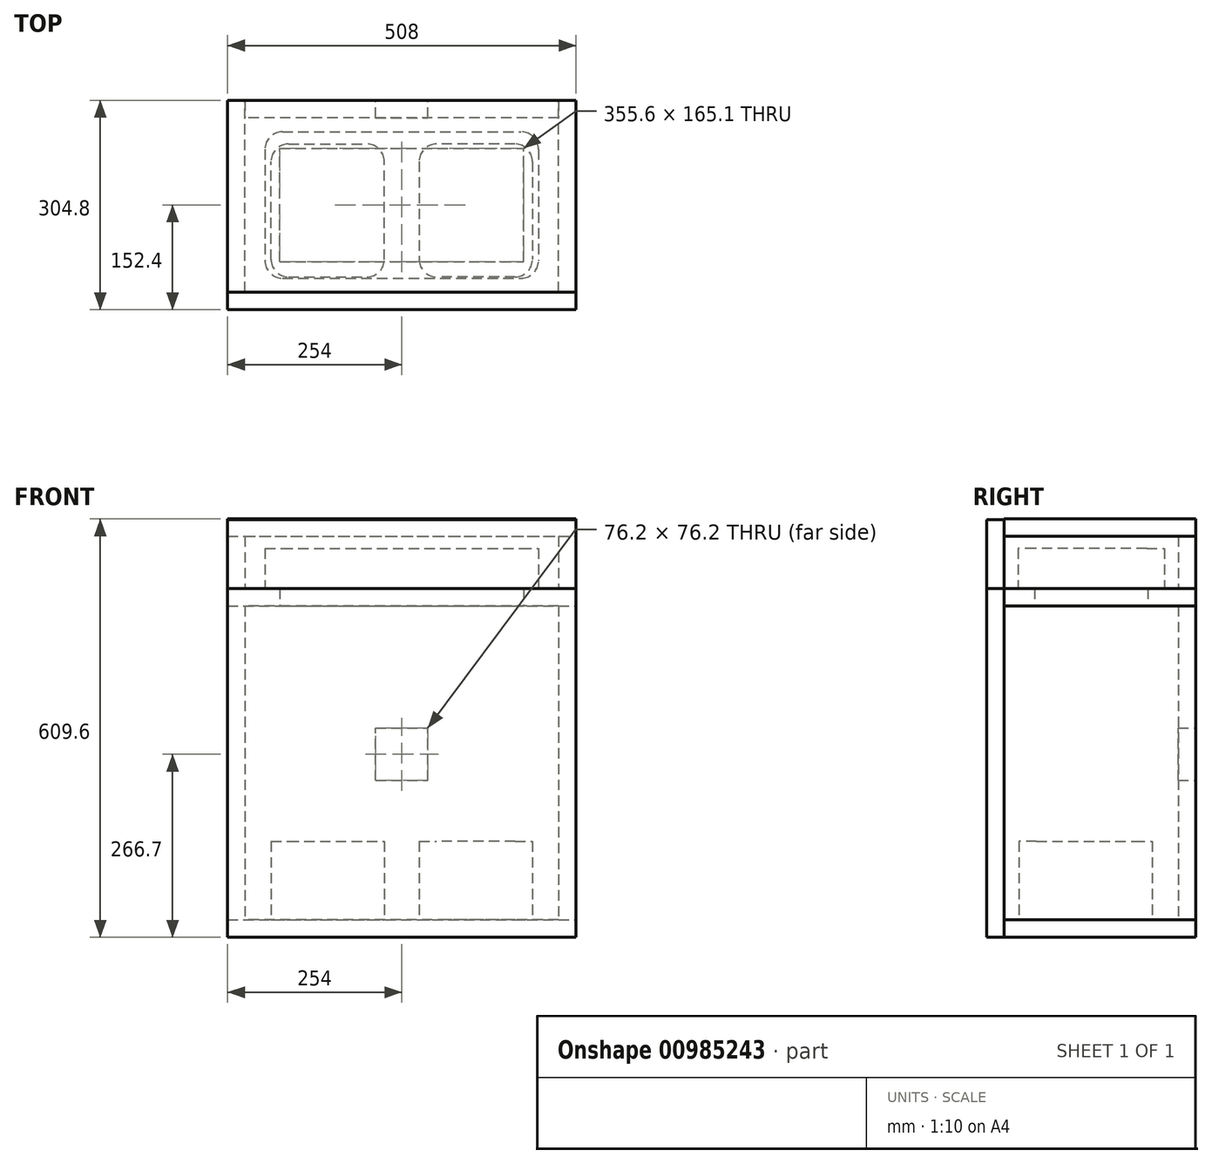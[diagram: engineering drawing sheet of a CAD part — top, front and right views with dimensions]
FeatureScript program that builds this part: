
annotation { "Feature Type Name" : "Feature", "Feature Type Description" : "" }
export const myFeature = defineFeature(function(context is Context, id is Id, definition is map)
    precondition{}
    {
        {
            var Q0;
            Q0=qCreatedBy(makeId("Top.planeOp"),FACE);
            var sketch = newSketch(context, id + "F0", { "sketchPlane" : qUnion([Q0])});
            skLineSegment(sketch, "E0.bottom", {"start": v(0, 0) * mm, "end": v(508, 0) * mm});
            skLineSegment(sketch, "E0.top", {"start": v(0, 279.4) * mm, "end": v(508, 279.4) * mm});
            skLineSegment(sketch, "E0.left", {"start": v(0, 0) * mm, "end": v(0, 279.4) * mm});
            skLineSegment(sketch, "E0.right", {"start": v(508, 0) * mm, "end": v(508, 279.4) * mm});
            skLineSegment(sketch, "E1.bottom", {"start": v(76.2, 44.45) * mm, "end": v(431.8, 44.45) * mm});
            skLineSegment(sketch, "E1.top", {"start": v(76.2, 209.55) * mm, "end": v(431.8, 209.55) * mm});
            skLineSegment(sketch, "E1.left", {"start": v(76.2, 44.45) * mm, "end": v(76.2, 209.55) * mm});
            skLineSegment(sketch, "E1.right", {"start": v(431.8, 44.45) * mm, "end": v(431.8, 209.55) * mm});
            skSolve(sketch);
        }
        {
            var Q0;
            Q0 = qSketchRegion(id + "F0", true);
            extrude(context, id + "F1", {"entities" : qUnion([Q0]), "depth" : 25.4 * mm, "offsetDistance" : 25.4 * mm});
        }
        {
            var Q0;
            Q0=makeQuery(id+"F1.opExtrude","CAP_FACE",FACE,{"disambiguationData":[OSD([sQuery(id+"F0.wireOp",EDGE,"E0.bottom"),sQuery(id+"F0.wireOp",EDGE,"E0.top"),sQuery(id+"F0.wireOp",EDGE,"E0.left"),sQuery(id+"F0.wireOp",EDGE,"E0.right"),sQuery(id+"F0.wireOp",EDGE,"E1.bottom"),sQuery(id+"F0.wireOp",EDGE,"E1.top"),sQuery(id+"F0.wireOp",EDGE,"E1.left"),sQuery(id+"F0.wireOp",EDGE,"E1.right")])],"isStart":false});
            var sketch = newSketch(context, id + "F2", { "sketchPlane" : qUnion([Q0])});
            skLineSegment(sketch, "E2.bottom", {"start": v(0, 0) * mm, "end": v(25.4, 0) * mm});
            skLineSegment(sketch, "E2.top", {"start": v(0, 279.4) * mm, "end": v(25.4, 279.4) * mm});
            skLineSegment(sketch, "E2.left", {"start": v(0, 0) * mm, "end": v(0, 279.4) * mm});
            skLineSegment(sketch, "E2.right", {"start": v(25.4, 0) * mm, "end": v(25.4, 279.4) * mm});
            skSolve(sketch);
        }
        {
            var Q0;
            Q0 = qSketchRegion(id + "F2", true);
            extrude(context, id + "F3", {"entities" : qUnion([Q0]), "depth" : 76.2 * mm, "offsetDistance" : 25.4 * mm});
        }
        {
            var Q0;
            Q0=makeQuery(id+"F1.opExtrude","CAP_FACE",FACE,{"disambiguationData":[OSD([sQuery(id+"F0.wireOp",EDGE,"E0.bottom"),sQuery(id+"F0.wireOp",EDGE,"E0.top"),sQuery(id+"F0.wireOp",EDGE,"E0.left"),sQuery(id+"F0.wireOp",EDGE,"E0.right"),sQuery(id+"F0.wireOp",EDGE,"E1.bottom"),sQuery(id+"F0.wireOp",EDGE,"E1.top"),sQuery(id+"F0.wireOp",EDGE,"E1.left"),sQuery(id+"F0.wireOp",EDGE,"E1.right")])],"isStart":false});
            var sketch = newSketch(context, id + "F4", { "sketchPlane" : qUnion([Q0])});
            skLineSegment(sketch, "E3.bottom", {"start": v(508, 0) * mm, "end": v(482.6, 0) * mm});
            skLineSegment(sketch, "E3.top", {"start": v(508, 279.4) * mm, "end": v(482.6, 279.4) * mm});
            skLineSegment(sketch, "E3.left", {"start": v(508, 0) * mm, "end": v(508, 279.4) * mm});
            skLineSegment(sketch, "E3.right", {"start": v(482.6, 0) * mm, "end": v(482.6, 279.4) * mm});
            skSolve(sketch);
        }
        {
            var Q0;
            Q0 = qSketchRegion(id + "F4", true);
            extrude(context, id + "F5", {"entities" : qUnion([Q0]), "depth" : 76.2 * mm, "offsetDistance" : 25.4 * mm});
        }
        {
            var Q0;
            Q0=makeQuery(id+"F1.opExtrude","CAP_FACE",FACE,{"disambiguationData":[OSD([sQuery(id+"F0.wireOp",EDGE,"E0.bottom"),sQuery(id+"F0.wireOp",EDGE,"E0.top"),sQuery(id+"F0.wireOp",EDGE,"E0.left"),sQuery(id+"F0.wireOp",EDGE,"E0.right"),sQuery(id+"F0.wireOp",EDGE,"E1.bottom"),sQuery(id+"F0.wireOp",EDGE,"E1.top"),sQuery(id+"F0.wireOp",EDGE,"E1.left"),sQuery(id+"F0.wireOp",EDGE,"E1.right")])],"isStart":false});
            var sketch = newSketch(context, id + "F6", { "sketchPlane" : qUnion([Q0])});
            skLineSegment(sketch, "E4.bottom", {"start": v(482.6, 279.4) * mm, "end": v(25.4, 279.4) * mm});
            skLineSegment(sketch, "E4.top", {"start": v(482.6, 254) * mm, "end": v(25.4, 254) * mm});
            skLineSegment(sketch, "E4.left", {"start": v(482.6, 279.4) * mm, "end": v(482.6, 254) * mm});
            skLineSegment(sketch, "E4.right", {"start": v(25.4, 279.4) * mm, "end": v(25.4, 254) * mm});
            skSolve(sketch);
        }
        {
            var Q0;
            Q0 = qSketchRegion(id + "F6", true);
            extrude(context, id + "F7", {"entities" : qUnion([Q0]), "depth" : 76.2 * mm, "offsetDistance" : 25.4 * mm});
        }
        {
            var Q0;
            Q0=makeQuery(id+"F1.opExtrude","CAP_FACE",FACE,{"disambiguationData":[OSD([sQuery(id+"F0.wireOp",EDGE,"E0.bottom"),sQuery(id+"F0.wireOp",EDGE,"E0.top"),sQuery(id+"F0.wireOp",EDGE,"E0.left"),sQuery(id+"F0.wireOp",EDGE,"E0.right"),sQuery(id+"F0.wireOp",EDGE,"E1.bottom"),sQuery(id+"F0.wireOp",EDGE,"E1.top"),sQuery(id+"F0.wireOp",EDGE,"E1.left"),sQuery(id+"F0.wireOp",EDGE,"E1.right")])],"isStart":false});
            var sketch = newSketch(context, id + "F8", { "sketchPlane" : qUnion([Q0])});
            skLineSegment(sketch, "E5.bottom", {"start": v(80, 233.68) * mm, "end": v(428, 233.68) * mm});
            skLineSegment(sketch, "E5.top", {"start": v(80, 20.32) * mm, "end": v(428, 20.32) * mm});
            skLineSegment(sketch, "E5.left", {"start": v(54.6, 208.28) * mm, "end": v(54.6, 45.72) * mm});
            skLineSegment(sketch, "E5.right", {"start": v(453.4, 208.28) * mm, "end": v(453.4, 45.72) * mm});
            skPoint(sketch, "E6.visualSharp", {"position": v(54.6, 233.68) * mm});
            skArc(sketch, "E6.filletArc", {"start": v(80, 233.68) * mm, "mid": v(62.05, 226.24) * mm, "end": v(54.6, 208.28) * mm});
            skPoint(sketch, "E7.visualSharp", {"position": v(54.6, 20.32) * mm});
            skArc(sketch, "E7.filletArc", {"start": v(54.6, 45.72) * mm, "mid": v(62.05, 27.76) * mm, "end": v(80, 20.32) * mm});
            skPoint(sketch, "E8.visualSharp", {"position": v(453.4, 20.32) * mm});
            skArc(sketch, "E8.filletArc", {"start": v(428, 20.32) * mm, "mid": v(445.95, 27.76) * mm, "end": v(453.4, 45.72) * mm});
            skPoint(sketch, "E9.visualSharp", {"position": v(453.4, 233.68) * mm});
            skArc(sketch, "E9.filletArc", {"start": v(453.4, 208.28) * mm, "mid": v(445.95, 226.24) * mm, "end": v(428, 233.68) * mm});
            skSolve(sketch);
        }
        {
            var Q0;
            Q0 = qSketchRegion(id + "F8", true);
            extrude(context, id + "F9", {"entities" : qUnion([Q0]), "depth" : 58.42 * mm, "offsetDistance" : 25.4 * mm});
        }
        {
            var Q0;
            Q0=makeQuery(id+"F3.opExtrude","CAP_FACE",FACE,{"disambiguationData":[OSD([sQuery(id+"F2.wireOp",EDGE,"E2.bottom"),sQuery(id+"F2.wireOp",EDGE,"E2.top"),sQuery(id+"F2.wireOp",EDGE,"E2.left"),sQuery(id+"F2.wireOp",EDGE,"E2.right")])],"isStart":false});
            var sketch = newSketch(context, id + "F10", { "sketchPlane" : qUnion([Q0])});
            skLineSegment(sketch, "E10.bottom", {"start": v(0, 0) * mm, "end": v(508, 0) * mm});
            skLineSegment(sketch, "E10.top", {"start": v(0, 279.4) * mm, "end": v(508, 279.4) * mm});
            skLineSegment(sketch, "E10.left", {"start": v(0, 0) * mm, "end": v(0, 279.4) * mm});
            skLineSegment(sketch, "E10.right", {"start": v(508, 0) * mm, "end": v(508, 279.4) * mm});
            skSolve(sketch);
        }
        {
            var Q0;
            Q0 = qSketchRegion(id + "F10", true);
            extrude(context, id + "F11", {"entities" : qUnion([Q0]), "depth" : 25.4 * mm, "offsetDistance" : 25.4 * mm});
        }
        {
            var Q0;
            Q0=makeQuery(id+"F1.opExtrude","CAP_FACE",FACE,{"disambiguationData":[OSD([sQuery(id+"F0.wireOp",EDGE,"E0.bottom"),sQuery(id+"F0.wireOp",EDGE,"E0.top"),sQuery(id+"F0.wireOp",EDGE,"E0.left"),sQuery(id+"F0.wireOp",EDGE,"E0.right"),sQuery(id+"F0.wireOp",EDGE,"E1.bottom"),sQuery(id+"F0.wireOp",EDGE,"E1.top"),sQuery(id+"F0.wireOp",EDGE,"E1.left"),sQuery(id+"F0.wireOp",EDGE,"E1.right")])],"isStart":true});
            var sketch = newSketch(context, id + "F12", { "sketchPlane" : qUnion([Q0])});
            skLineSegment(sketch, "E11.bottom", {"start": v(0, -279.4) * mm, "end": v(25.4, -279.4) * mm});
            skLineSegment(sketch, "E11.top", {"start": v(0, 0) * mm, "end": v(25.4, 0) * mm});
            skLineSegment(sketch, "E11.left", {"start": v(0, -279.4) * mm, "end": v(0, 0) * mm});
            skLineSegment(sketch, "E11.right", {"start": v(25.4, -279.4) * mm, "end": v(25.4, 0) * mm});
            skSolve(sketch);
        }
        {
            var Q0;
            Q0 = qSketchRegion(id + "F12", true);
            extrude(context, id + "F13", {"entities" : qUnion([Q0]), "depth" : 457.2 * mm, "offsetDistance" : 25.4 * mm});
        }
        {
            var Q0;
            Q0=makeQuery(id+"F1.opExtrude","CAP_FACE",FACE,{"disambiguationData":[OSD([sQuery(id+"F0.wireOp",EDGE,"E0.bottom"),sQuery(id+"F0.wireOp",EDGE,"E0.top"),sQuery(id+"F0.wireOp",EDGE,"E0.left"),sQuery(id+"F0.wireOp",EDGE,"E0.right"),sQuery(id+"F0.wireOp",EDGE,"E1.bottom"),sQuery(id+"F0.wireOp",EDGE,"E1.top"),sQuery(id+"F0.wireOp",EDGE,"E1.left"),sQuery(id+"F0.wireOp",EDGE,"E1.right")])],"isStart":true});
            var sketch = newSketch(context, id + "F14", { "sketchPlane" : qUnion([Q0])});
            skLineSegment(sketch, "E12.bottom", {"start": v(508, -279.4) * mm, "end": v(482.6, -279.4) * mm});
            skLineSegment(sketch, "E12.top", {"start": v(508, 0) * mm, "end": v(482.6, 0) * mm});
            skLineSegment(sketch, "E12.left", {"start": v(508, -279.4) * mm, "end": v(508, 0) * mm});
            skLineSegment(sketch, "E12.right", {"start": v(482.6, -279.4) * mm, "end": v(482.6, 0) * mm});
            skSolve(sketch);
        }
        {
            var Q0;
            Q0 = qSketchRegion(id + "F14", true);
            extrude(context, id + "F15", {"entities" : qUnion([Q0]), "depth" : 457.2 * mm, "offsetDistance" : 25.4 * mm});
        }
        {
            var Q0;
            Q0=makeQuery(id+"F13.opExtrude","CAP_FACE",FACE,{"disambiguationData":[OSD([sQuery(id+"F12.wireOp",EDGE,"E11.bottom"),sQuery(id+"F12.wireOp",EDGE,"E11.top"),sQuery(id+"F12.wireOp",EDGE,"E11.left"),sQuery(id+"F12.wireOp",EDGE,"E11.right")])],"isStart":false});
            var sketch = newSketch(context, id + "F16", { "sketchPlane" : qUnion([Q0])});
            skLineSegment(sketch, "E13.bottom", {"start": v(0, 0) * mm, "end": v(508, 0) * mm});
            skLineSegment(sketch, "E13.top", {"start": v(0, -279.4) * mm, "end": v(508, -279.4) * mm});
            skLineSegment(sketch, "E13.left", {"start": v(0, 0) * mm, "end": v(0, -279.4) * mm});
            skLineSegment(sketch, "E13.right", {"start": v(508, 0) * mm, "end": v(508, -279.4) * mm});
            skSolve(sketch);
        }
        {
            var Q0;
            Q0 = qSketchRegion(id + "F16", true);
            extrude(context, id + "F17", {"entities" : qUnion([Q0]), "depth" : 25.4 * mm, "offsetDistance" : 25.4 * mm});
        }
        {
            var Q0;
            Q0=makeQuery(id+"F13.opExtrude","SWEPT_FACE",FACE,{"disambiguationData":[OSD([sQuery(id+"F12.wireOp",EDGE,"E11.right")])]});
            var sketch = newSketch(context, id + "F18", { "sketchPlane" : qUnion([Q0])});
            skLineSegment(sketch, "E14.bottom", {"start": v(279.4, 0) * mm, "end": v(254, 0) * mm});
            skLineSegment(sketch, "E14.top", {"start": v(279.4, -457.2) * mm, "end": v(254, -457.2) * mm});
            skLineSegment(sketch, "E14.left", {"start": v(279.4, 0) * mm, "end": v(279.4, -457.2) * mm});
            skLineSegment(sketch, "E14.right", {"start": v(254, 0) * mm, "end": v(254, -457.2) * mm});
            skSolve(sketch);
        }
        {
            var Q0;
            Q0 = qSketchRegion(id + "F18", true);
            extrude(context, id + "F19", {"entities" : qUnion([Q0]), "depth" : 457.2 * mm, "offsetDistance" : 25.4 * mm});
        }
        {
            var Q0;
            Q0=makeQuery(id+"F17.opExtrude","SWEPT_FACE",FACE,{"disambiguationData":[OSD([sQuery(id+"F16.wireOp",EDGE,"E13.bottom")])]});
            var sketch = newSketch(context, id + "F20", { "sketchPlane" : qUnion([Q0])});
            skLineSegment(sketch, "E15.bottom", {"start": v(0, -482.6) * mm, "end": v(508, -482.6) * mm});
            skLineSegment(sketch, "E15.top", {"start": v(0, 25.4) * mm, "end": v(508, 25.4) * mm});
            skLineSegment(sketch, "E15.left", {"start": v(0, -482.6) * mm, "end": v(0, 25.4) * mm});
            skLineSegment(sketch, "E15.right", {"start": v(508, -482.6) * mm, "end": v(508, 25.4) * mm});
            skSolve(sketch);
        }
        {
            var Q0;
            Q0 = qSketchRegion(id + "F20", true);
            extrude(context, id + "F21", {"entities" : qUnion([Q0]), "depth" : 25.4 * mm, "offsetDistance" : 25.4 * mm});
        }
        {
            var Q0;
            Q0=makeQuery(id+"F3.opExtrude","SWEPT_FACE",FACE,{"disambiguationData":[OSD([sQuery(id+"F2.wireOp",EDGE,"E2.bottom")])]});
            var sketch = newSketch(context, id + "F22", { "sketchPlane" : qUnion([Q0])});
            skLineSegment(sketch, "E16.bottom", {"start": v(0, 25.4) * mm, "end": v(508, 25.4) * mm});
            skLineSegment(sketch, "E16.top", {"start": v(0, 125.75) * mm, "end": v(508, 125.75) * mm});
            skLineSegment(sketch, "E16.left", {"start": v(0, 25.4) * mm, "end": v(0, 125.75) * mm});
            skLineSegment(sketch, "E16.right", {"start": v(508, 25.4) * mm, "end": v(508, 125.75) * mm});
            skSolve(sketch);
        }
        {
            var Q0;
            Q0 = qSketchRegion(id + "F22", true);
            extrude(context, id + "F23", {"entities" : qUnion([Q0]), "depth" : 25.4 * mm, "offsetDistance" : 25.4 * mm});
        }
        {
            var Q0;
            Q0=makeQuery(id+"F19.opExtrude","SWEPT_FACE",FACE,{"disambiguationData":[OSD([sQuery(id+"F18.wireOp",EDGE,"E14.left")])]});
            var sketch = newSketch(context, id + "F24", { "sketchPlane" : qUnion([Q0])});
            skLineSegment(sketch, "E17.bottom", {"start": v(-292.1, -177.8) * mm, "end": v(-215.9, -177.8) * mm});
            skLineSegment(sketch, "E17.top", {"start": v(-292.1, -254) * mm, "end": v(-215.9, -254) * mm});
            skLineSegment(sketch, "E17.left", {"start": v(-292.1, -177.8) * mm, "end": v(-292.1, -254) * mm});
            skLineSegment(sketch, "E17.right", {"start": v(-215.9, -177.8) * mm, "end": v(-215.9, -254) * mm});
            skSolve(sketch);
        }
        {
            var Q0;
            Q0 = qSketchRegion(id + "F24", true);
            extrude(context, id + "F25", {"entities" : qUnion([Q0]), "operationType" : NewBodyOperationType.REMOVE, "endBound" : BoundingType.UP_TO_NEXT, "oppositeDirection" : true, "depth" : 25.4 * mm, "offsetDistance" : 25.4 * mm});
        }
        {
            var Q0;
            Q0=makeQuery(id+"F17.opExtrude","CAP_FACE",FACE,{"disambiguationData":[OSD([sQuery(id+"F16.wireOp",EDGE,"E13.bottom"),sQuery(id+"F16.wireOp",EDGE,"E13.top"),sQuery(id+"F16.wireOp",EDGE,"E13.left"),sQuery(id+"F16.wireOp",EDGE,"E13.right")])],"isStart":true});
            var sketch = newSketch(context, id + "F26", { "sketchPlane" : qUnion([Q0])});
            skLineSegment(sketch, "E18.bottom", {"start": v(88.9, 22.1) * mm, "end": v(203.2, 22.1) * mm});
            skLineSegment(sketch, "E18.top", {"start": v(88.9, 215.9) * mm, "end": v(203.2, 215.9) * mm});
            skLineSegment(sketch, "E18.left", {"start": v(63.5, 47.5) * mm, "end": v(63.5, 190.5) * mm});
            skLineSegment(sketch, "E18.right", {"start": v(228.6, 47.5) * mm, "end": v(228.6, 190.5) * mm});
            skLineSegment(sketch, "E19", {"start": v(228.6, 215.9) * mm, "end": v(454.58, 215.9) * mm, "construction": true});
            skLineSegment(sketch, "E20", {"start": v(228.6, 22.1) * mm, "end": v(467.18, 22.1) * mm, "construction": true});
            skLineSegment(sketch, "E21.bottom", {"start": v(419.1, 215.9) * mm, "end": v(304.8, 215.9) * mm});
            skLineSegment(sketch, "E21.top", {"start": v(419.1, 22.1) * mm, "end": v(304.8, 22.1) * mm});
            skLineSegment(sketch, "E21.left", {"start": v(444.5, 190.5) * mm, "end": v(444.5, 47.5) * mm});
            skLineSegment(sketch, "E21.right", {"start": v(279.4, 190.5) * mm, "end": v(279.4, 47.5) * mm});
            skPoint(sketch, "E22.visualSharp", {"position": v(63.5, 215.9) * mm});
            skArc(sketch, "E22.filletArc", {"start": v(88.9, 215.9) * mm, "mid": v(70.94, 208.46) * mm, "end": v(63.5, 190.5) * mm});
            skPoint(sketch, "E23.visualSharp", {"position": v(63.5, 22.1) * mm});
            skArc(sketch, "E23.filletArc", {"start": v(63.5, 47.5) * mm, "mid": v(70.94, 29.54) * mm, "end": v(88.9, 22.1) * mm});
            skPoint(sketch, "E24.visualSharp", {"position": v(228.6, 22.1) * mm});
            skArc(sketch, "E24.filletArc", {"start": v(203.2, 22.1) * mm, "mid": v(221.16, 29.54) * mm, "end": v(228.6, 47.5) * mm});
            skPoint(sketch, "E25.visualSharp", {"position": v(228.6, 215.9) * mm});
            skArc(sketch, "E25.filletArc", {"start": v(228.6, 190.5) * mm, "mid": v(221.16, 208.46) * mm, "end": v(203.2, 215.9) * mm});
            skPoint(sketch, "E26.visualSharp", {"position": v(279.4, 215.9) * mm});
            skArc(sketch, "E26.filletArc", {"start": v(304.8, 215.9) * mm, "mid": v(286.84, 208.46) * mm, "end": v(279.4, 190.5) * mm});
            skPoint(sketch, "E27.visualSharp", {"position": v(279.4, 22.1) * mm});
            skArc(sketch, "E27.filletArc", {"start": v(279.4, 47.5) * mm, "mid": v(286.84, 29.54) * mm, "end": v(304.8, 22.1) * mm});
            skPoint(sketch, "E28.visualSharp", {"position": v(444.5, 22.1) * mm});
            skArc(sketch, "E28.filletArc", {"start": v(419.1, 22.1) * mm, "mid": v(437.06, 29.54) * mm, "end": v(444.5, 47.5) * mm});
            skPoint(sketch, "E29.visualSharp", {"position": v(444.5, 215.9) * mm});
            skArc(sketch, "E29.filletArc", {"start": v(444.5, 190.5) * mm, "mid": v(437.06, 208.46) * mm, "end": v(419.1, 215.9) * mm});
            skSolve(sketch);
        }
        {
            var Q0;
            Q0 = qSketchRegion(id + "F26", true);
            extrude(context, id + "F27", {"entities" : qUnion([Q0]), "depth" : 114.3 * mm, "offsetDistance" : 25.4 * mm});
        }
    });
